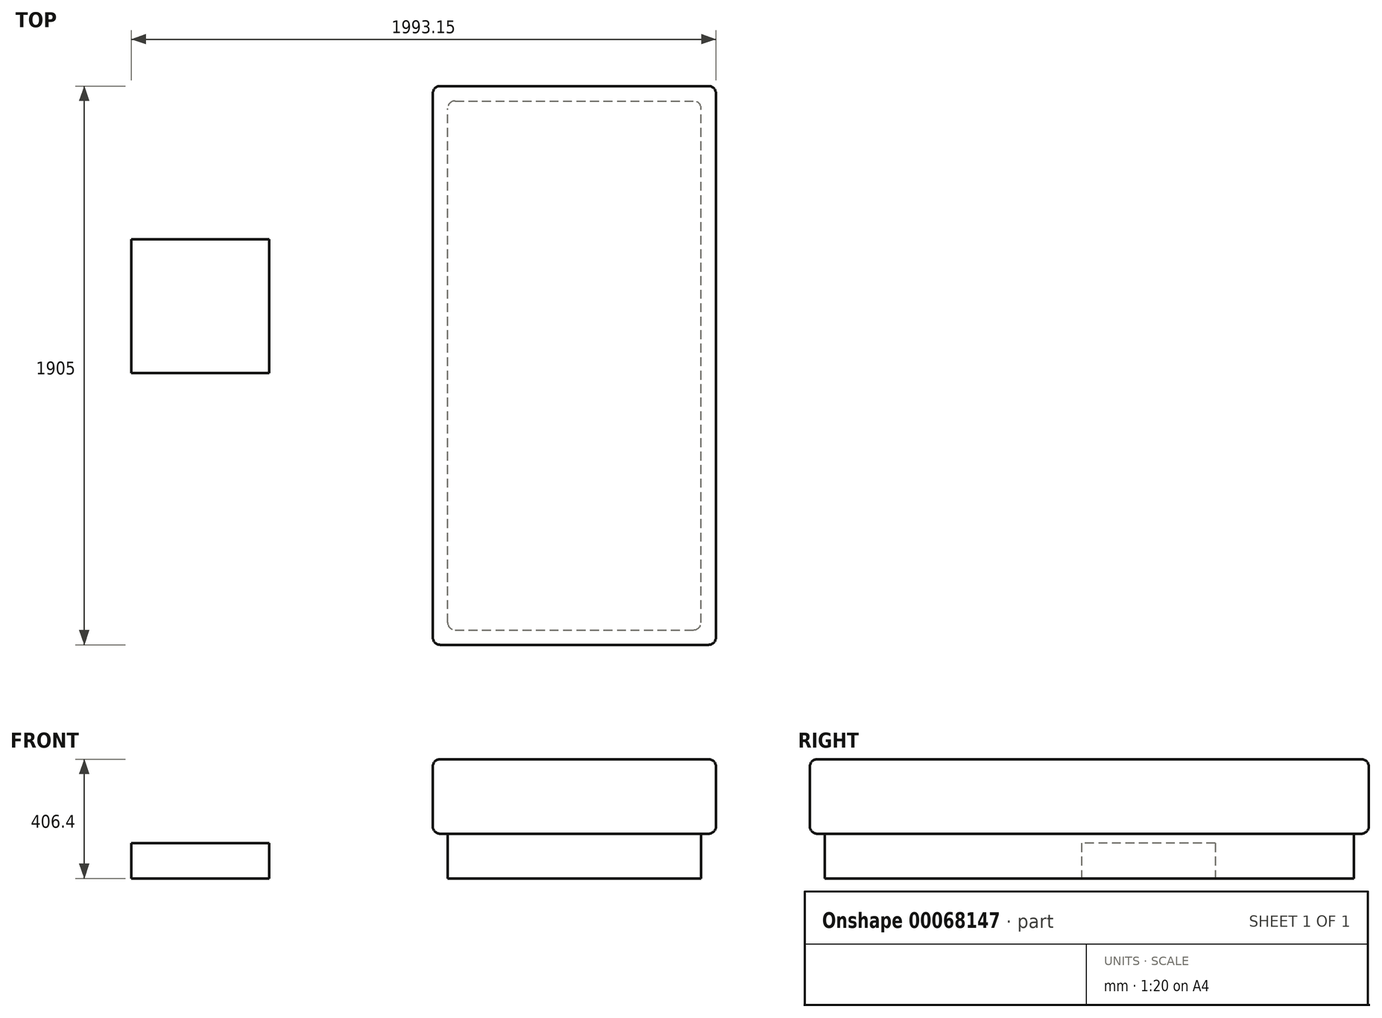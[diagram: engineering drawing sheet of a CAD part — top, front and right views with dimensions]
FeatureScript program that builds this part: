
annotation { "Feature Type Name" : "Feature", "Feature Type Description" : "" }
export const myFeature = defineFeature(function(context is Context, id is Id, definition is map)
    precondition{}
    {
        {
            var Q0;
            Q0=qCreatedBy(makeId("Top.planeOp"),FACE);
            var sketch = newSketch(context, id + "F0", { "sketchPlane" : qUnion([Q0])});
            skLineSegment(sketch, "E0.bottom", {"start": v(-464.48, -875.16) * mm, "end": v(399.12, -875.16) * mm});
            skLineSegment(sketch, "E0.top", {"start": v(-464.48, 928.24) * mm, "end": v(399.12, 928.24) * mm});
            skLineSegment(sketch, "E0.left", {"start": v(-464.48, -875.16) * mm, "end": v(-464.48, 928.24) * mm});
            skLineSegment(sketch, "E0.right", {"start": v(399.12, -875.16) * mm, "end": v(399.12, 928.24) * mm});
            skSolve(sketch);
        }
        {
            var Q0;
            Q0 = qSketchRegion(id + "F0", true);
            extrude(context, id + "F1", {"entities" : qUnion([Q0]), "depth" : 152.4 * mm});
        }
        {
            var Q0;
            Q0=makeQuery(id+"F1.opExtrude","CAP_FACE",FACE,{"disambiguationData":[OSD([sQuery(id+"F0.wireOp",EDGE,"E0.bottom"),sQuery(id+"F0.wireOp",EDGE,"E0.top"),sQuery(id+"F0.wireOp",EDGE,"E0.left"),sQuery(id+"F0.wireOp",EDGE,"E0.right")])],"isStart":false});
            var sketch = newSketch(context, id + "F2", { "sketchPlane" : qUnion([Q0])});
            skLineSegment(sketch, "E1.0", {"start": v(-515.28, -925.96) * mm, "end": v(-515.28, 979.04) * mm});
            skLineSegment(sketch, "E1.1", {"start": v(-515.28, -925.96) * mm, "end": v(449.92, -925.96) * mm});
            skLineSegment(sketch, "E1.2", {"start": v(449.92, -925.96) * mm, "end": v(449.92, 979.04) * mm});
            skLineSegment(sketch, "E1.3", {"start": v(-515.28, 979.04) * mm, "end": v(449.92, 979.04) * mm});
            skSolve(sketch);
        }
        {
            var Q0;
            Q0 = qSketchRegion(id + "F2", true);
            extrude(context, id + "F3", {"entities" : qUnion([Q0]), "operationType" : NewBodyOperationType.ADD, "depth" : 254 * mm});
        }
        {
            var Q0;
            Q0=makeQuery(id+"F3.opExtrude","CAP_FACE",FACE,{"disambiguationData":[OSD([sQuery(id+"F2.wireOp",EDGE,"E1.0"),sQuery(id+"F2.wireOp",EDGE,"E1.1"),sQuery(id+"F2.wireOp",EDGE,"E1.2"),sQuery(id+"F2.wireOp",EDGE,"E1.3")])],"isStart":false});
            var Q1;
            Q1=makeQuery(id+"F3.opExtrude","SWEPT_FACE",FACE,{"disambiguationData":[OSD([sQuery(id+"F2.wireOp",EDGE,"E1.2")])]});
            var Q2;
            Q2=makeQuery(id+"F3.opExtrude","SWEPT_FACE",FACE,{"disambiguationData":[OSD([sQuery(id+"F2.wireOp",EDGE,"E1.3")])]});
            var Q3;
            Q3=makeQuery(id+"F3.opExtrude","SWEPT_FACE",FACE,{"disambiguationData":[OSD([sQuery(id+"F2.wireOp",EDGE,"E1.0")])]});
            var Q4;
            Q4=makeQuery(id+"F3.opExtrude","SWEPT_FACE",FACE,{"disambiguationData":[OSD([sQuery(id+"F2.wireOp",EDGE,"E1.1")])]});
            var Q5;
            Q5=makeQuery(id+"F1.opExtrude","SWEPT_EDGE",EDGE,{"disambiguationData":[OSD([sQuery(id+"F0.wireOp",EDGE,"E0.bottom"),sQuery(id+"F0.wireOp",EDGE,"E0.right")])]});
            var Q6;
            Q6=makeQuery(id+"F1.opExtrude","SWEPT_EDGE",EDGE,{"disambiguationData":[OSD([sQuery(id+"F0.wireOp",EDGE,"E0.top"),sQuery(id+"F0.wireOp",EDGE,"E0.right")])]});
            var Q7;
            Q7=makeQuery(id+"F1.opExtrude","SWEPT_EDGE",EDGE,{"disambiguationData":[OSD([sQuery(id+"F0.wireOp",EDGE,"E0.top"),sQuery(id+"F0.wireOp",EDGE,"E0.left")])]});
            var Q8;
            Q8=makeQuery(id+"F1.opExtrude","SWEPT_EDGE",EDGE,{"disambiguationData":[OSD([sQuery(id+"F0.wireOp",EDGE,"E0.bottom"),sQuery(id+"F0.wireOp",EDGE,"E0.left")])]});
            fillet(context, id + "F4", {"entities" : qUnion([Q0, Q1, Q2, Q3, Q4, Q5, Q6, Q7, Q8]), "radius" : 25.4 * mm, "tangentPropagation" : true, "allowEdgeOverflow" : false});
        }
        {
            var Q0;
            Q0=qCreatedBy(makeId("Top.planeOp"),FACE);
            var sketch = newSketch(context, id + "F5", { "sketchPlane" : qUnion([Q0])});
            skLineSegment(sketch, "E2.bottom", {"start": v(-1543.23, 455.9) * mm, "end": v(-1072.9, 455.9) * mm});
            skLineSegment(sketch, "E2.top", {"start": v(-1543.23, 0) * mm, "end": v(-1072.9, 0) * mm});
            skLineSegment(sketch, "E2.left", {"start": v(-1543.23, 455.9) * mm, "end": v(-1543.23, 0) * mm});
            skLineSegment(sketch, "E2.right", {"start": v(-1072.9, 455.9) * mm, "end": v(-1072.9, 0) * mm});
            skSolve(sketch);
        }
        {
            var Q0;
            Q0 = qSketchRegion(id + "F5", true);
            extrude(context, id + "F6", {"entities" : qUnion([Q0]), "depth" : 119.97 * mm});
        }
    });
